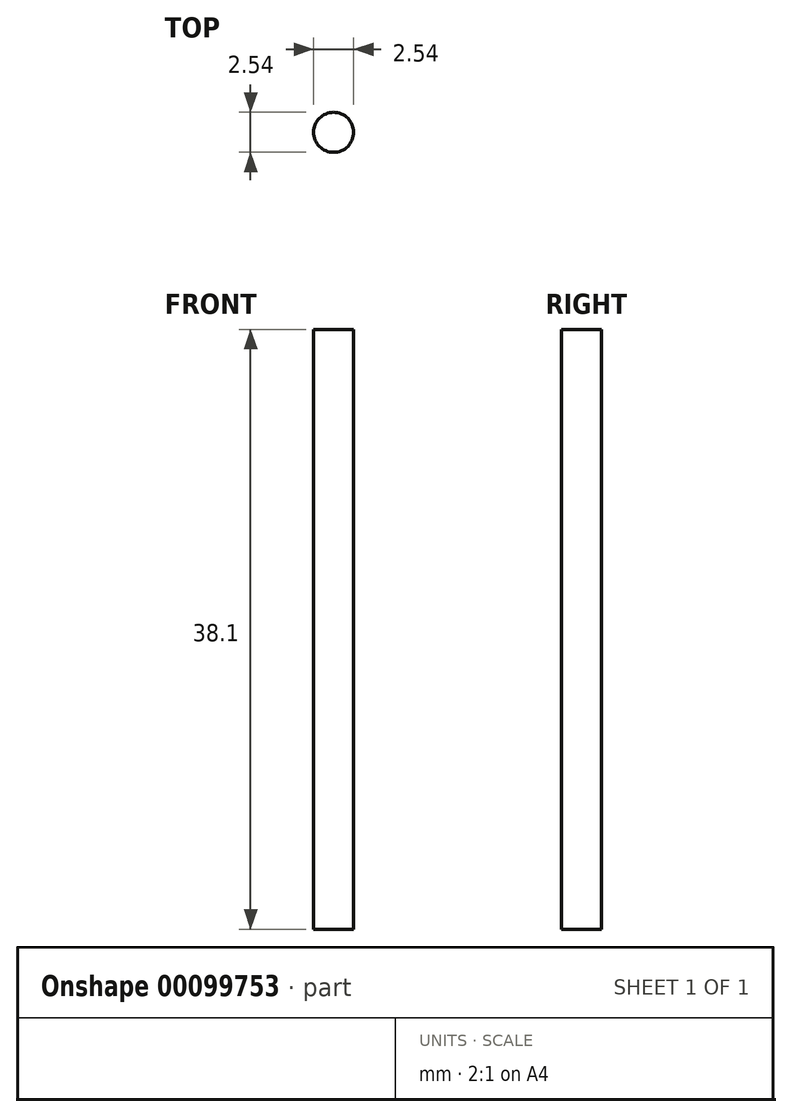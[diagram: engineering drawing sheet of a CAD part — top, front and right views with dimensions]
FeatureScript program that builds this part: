
annotation { "Feature Type Name" : "Feature", "Feature Type Description" : "" }
export const myFeature = defineFeature(function(context is Context, id is Id, definition is map)
    precondition{}
    {
        {
            var Q0;
            Q0=qCreatedBy(makeId("Top.planeOp"),FACE);
            var sketch = newSketch(context, id + "F0", { "sketchPlane" : qUnion([Q0])});
            skCircle(sketch, "E0", {"center": v(0, 0) * mm, "radius": 1.27 * mm});
            skSolve(sketch);
        }
        {
            var Q0;
            Q0=makeQuery(id+"F0.imprint","IMPRINT",FACE,{"disambiguationData":[TD([[makeQuery(id+"F0.imprint","IMPRINT",EDGE,{"derivedFrom":sQuery(id+"F0.wireOp",EDGE,"E0")}),1.0]])]});
            extrude(context, id + "F1", {"entities" : qUnion([Q0]), "depth" : 38.1 * mm});
        }
    });
